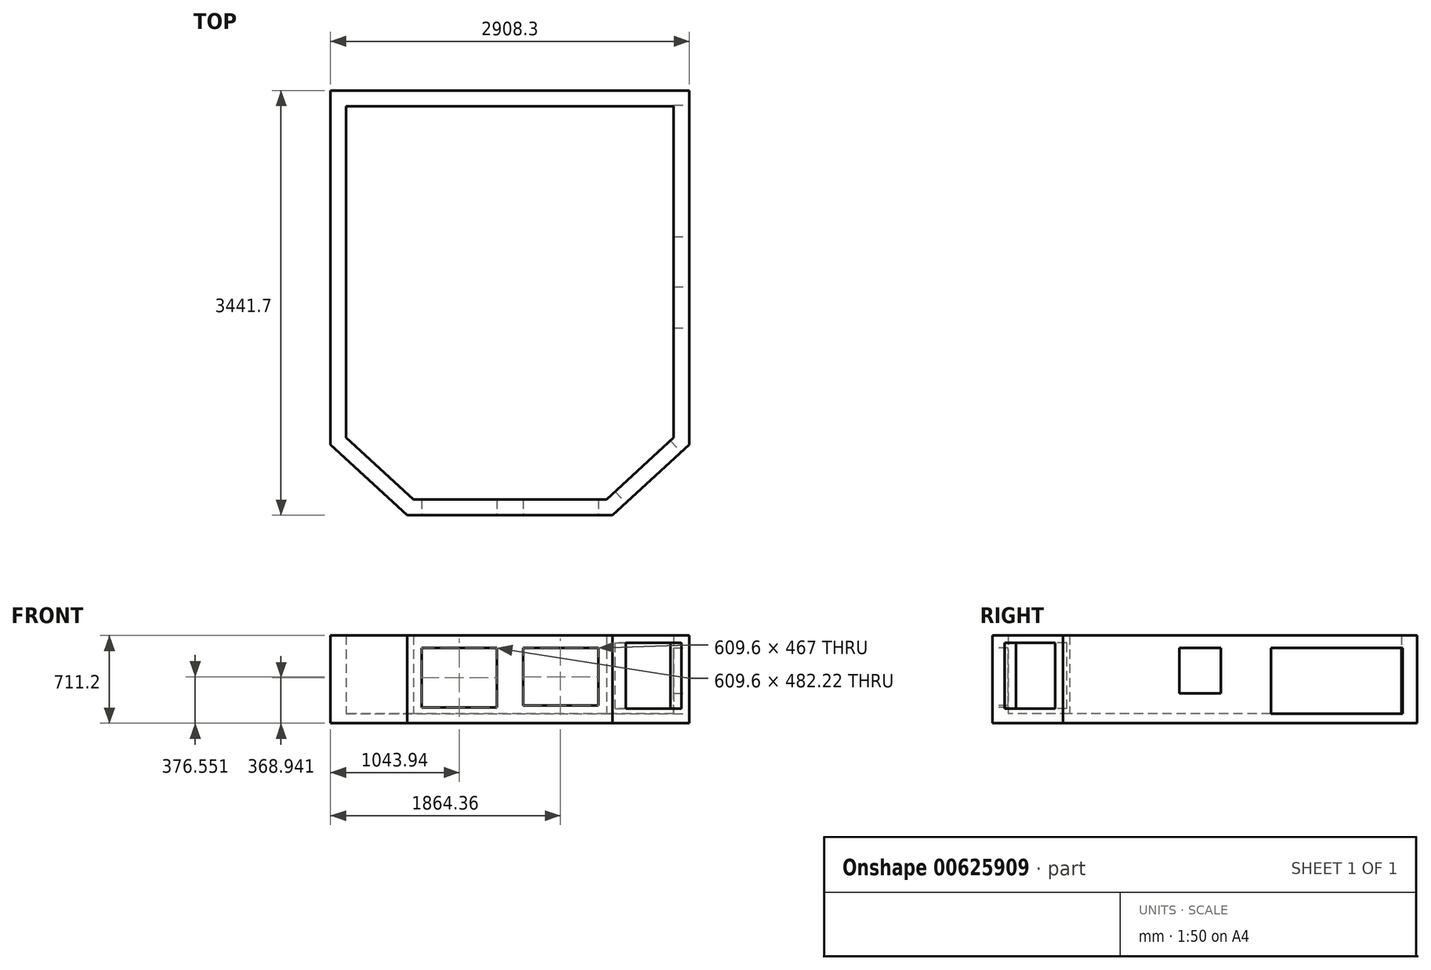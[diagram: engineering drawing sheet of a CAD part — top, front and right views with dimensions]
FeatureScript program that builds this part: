
annotation { "Feature Type Name" : "Feature", "Feature Type Description" : "" }
export const myFeature = defineFeature(function(context is Context, id is Id, definition is map)
    precondition{}
    {
        {
            var Q0;
            Q0=qCreatedBy(makeId("Top.planeOp"),FACE);
            var sketch = newSketch(context, id + "F0", { "sketchPlane" : qUnion([Q0])});
            skLineSegment(sketch, "E0", {"start": v(0, 0) * mm, "end": v(2908.3, 0) * mm});
            skLineSegment(sketch, "E1", {"start": v(2908.3, 0) * mm, "end": v(2908.3, -2870.2) * mm});
            skLineSegment(sketch, "E2", {"start": v(2908.3, -2870.2) * mm, "end": v(2286, -3441.7) * mm});
            skLineSegment(sketch, "E3", {"start": v(2286, -3441.7) * mm, "end": v(622.3, -3441.7) * mm});
            skLineSegment(sketch, "E4", {"start": v(622.3, -3441.7) * mm, "end": v(0, -2870.2) * mm});
            skLineSegment(sketch, "E5", {"start": v(0, 0) * mm, "end": v(0, -2870.2) * mm});
            skSolve(sketch);
        }
        {
            var Q0;
            Q0=makeQuery(id+"F0.imprint","IMPRINT",FACE,{"disambiguationData":[TD([[makeQuery(id+"F0.imprint","IMPRINT",EDGE,{"derivedFrom":sQuery(id+"F0.wireOp",EDGE,"E0")}),-1.0]])]});
            extrude(context, id + "F1", {"entities" : qUnion([Q0]), "oppositeDirection" : true, "depth" : 76.2 * mm, "offsetDistance" : 25.4 * mm});
        }
        {
            var Q0;
            Q0=makeQuery(id+"F1.opExtrude","CAP_FACE",FACE,{"disambiguationData":[OSD([sQuery(id+"F0.wireOp",EDGE,"E0"),sQuery(id+"F0.wireOp",EDGE,"E1"),sQuery(id+"F0.wireOp",EDGE,"E2"),sQuery(id+"F0.wireOp",EDGE,"E3"),sQuery(id+"F0.wireOp",EDGE,"E4"),sQuery(id+"F0.wireOp",EDGE,"E5")])],"isStart":true});
            var sketch = newSketch(context, id + "F2", { "sketchPlane" : qUnion([Q0])});
            skLineSegment(sketch, "E6.0", {"start": v(127, -127) * mm, "end": v(127, -2814.4) * mm});
            skLineSegment(sketch, "E6.1", {"start": v(2781.3, -127) * mm, "end": v(2781.3, -2814.4) * mm});
            skLineSegment(sketch, "E6.2", {"start": v(2781.3, -2814.4) * mm, "end": v(2236.53, -3314.7) * mm});
            skLineSegment(sketch, "E6.3", {"start": v(127, -127) * mm, "end": v(2781.3, -127) * mm});
            skLineSegment(sketch, "E6.4", {"start": v(2236.53, -3314.7) * mm, "end": v(671.77, -3314.7) * mm});
            skLineSegment(sketch, "E6.5", {"start": v(671.77, -3314.7) * mm, "end": v(127, -2814.4) * mm});
            skSolve(sketch);
        }
        {
            var Q0;
            Q0=makeQuery(id+"F2.imprint","IMPRINT",FACE,{"disambiguationData":[TD([[makeQuery(id+"F2.imprint","IMPRINT",EDGE,{"derivedFrom":sQuery(id+"F2.wireOp",EDGE,"E6.0")}),-1.0]])]});
            extrude(context, id + "F3", {"entities" : qUnion([Q0]), "operationType" : NewBodyOperationType.ADD, "depth" : 635 * mm, "offsetDistance" : 25.4 * mm});
        }
        {
            var Q0;
            {var subQ0=sQuery(id+"F0.wireOp",EDGE,"E1");Q0=makeQuery(id+"F3.boolean.opBoolean","MERGE",FACE,{"derivedFrom":[makeQuery(id+"F1.opExtrude","SWEPT_FACE",FACE,{"disambiguationData":[OSD([subQ0])]}),makeQuery(id+"F3.opExtrude","SWEPT_FACE",FACE,{"disambiguationData":[OSD([subQ0])]})]});}
            var sketch = newSketch(context, id + "F4", { "sketchPlane" : qUnion([Q0])});
            skLineSegment(sketch, "E7.bottom", {"start": v(-1925.32, 533.4) * mm, "end": v(-1590.04, 533.4) * mm});
            skLineSegment(sketch, "E7.top", {"start": v(-1925.32, 165.1) * mm, "end": v(-1590.04, 165.1) * mm});
            skLineSegment(sketch, "E7.left", {"start": v(-1925.32, 533.4) * mm, "end": v(-1925.32, 165.1) * mm});
            skLineSegment(sketch, "E7.right", {"start": v(-1590.04, 533.4) * mm, "end": v(-1590.04, 165.1) * mm});
            skLineSegment(sketch, "E8.bottom", {"start": v(-1183.64, 533.4) * mm, "end": v(-116.84, 533.4) * mm});
            skLineSegment(sketch, "E8.top", {"start": v(-1183.64, 0) * mm, "end": v(-116.84, 0) * mm});
            skLineSegment(sketch, "E8.left", {"start": v(-1183.64, 533.4) * mm, "end": v(-1183.64, 0) * mm});
            skLineSegment(sketch, "E8.right", {"start": v(-116.84, 533.4) * mm, "end": v(-116.84, 0) * mm});
            skSolve(sketch);
        }
        {
            var Q0;
            {var subQ0=sQuery(id+"F0.wireOp",EDGE,"E2");Q0=makeQuery(id+"F3.boolean.opBoolean","MERGE",FACE,{"derivedFrom":[makeQuery(id+"F1.opExtrude","SWEPT_FACE",FACE,{"disambiguationData":[OSD([subQ0])]}),makeQuery(id+"F3.opExtrude","SWEPT_FACE",FACE,{"disambiguationData":[OSD([subQ0])]})]});}
            var sketch = newSketch(context, id + "F5", { "sketchPlane" : qUnion([Q0])});
            skLineSegment(sketch, "E9.bottom", {"start": v(-498.63, 573.72) * mm, "end": v(110.97, 573.72) * mm});
            skLineSegment(sketch, "E9.top", {"start": v(-498.63, 40.32) * mm, "end": v(110.97, 40.32) * mm});
            skLineSegment(sketch, "E9.left", {"start": v(-498.63, 573.72) * mm, "end": v(-498.63, 40.32) * mm});
            skLineSegment(sketch, "E9.right", {"start": v(110.97, 573.72) * mm, "end": v(110.97, 40.32) * mm});
            skSolve(sketch);
        }
        {
            var Q0;
            Q0=makeQuery(id+"F4.imprint","IMPRINT",FACE,{"disambiguationData":[TD([[makeQuery(id+"F4.imprint","IMPRINT",EDGE,{"derivedFrom":sQuery(id+"F4.wireOp",EDGE,"E8.bottom")}),-1.0]])]});
            var Q1;
            Q1=makeQuery(id+"F4.imprint","IMPRINT",FACE,{"disambiguationData":[TD([[makeQuery(id+"F4.imprint","IMPRINT",EDGE,{"derivedFrom":sQuery(id+"F4.wireOp",EDGE,"E7.bottom")}),-1.0]])]});
            var Q2;
            Q2=makeQuery(id+"F3.opExtrude","SWEPT_FACE",FACE,{"disambiguationData":[OSD([sQuery(id+"F2.wireOp",EDGE,"E6.1")])]});
            extrude(context, id + "F6", {"entities" : qUnion([Q0, Q1]), "operationType" : NewBodyOperationType.REMOVE, "endBound" : BoundingType.UP_TO_SURFACE, "oppositeDirection" : true, "depth" : 25.4 * mm, "endBoundEntityFace" : qUnion([Q2]), "offsetDistance" : 25.4 * mm});
        }
        {
            var Q0;
            Q0=makeQuery(id+"F5.imprint","IMPRINT",FACE,{"disambiguationData":[TD([[makeQuery(id+"F5.imprint","IMPRINT",EDGE,{"derivedFrom":sQuery(id+"F5.wireOp",EDGE,"E9.bottom")}),-1.0]])]});
            var Q1;
            Q1=makeQuery(id+"F3.opExtrude","SWEPT_FACE",FACE,{"disambiguationData":[OSD([sQuery(id+"F2.wireOp",EDGE,"E6.2")])]});
            extrude(context, id + "F7", {"entities" : qUnion([Q0]), "operationType" : NewBodyOperationType.REMOVE, "endBound" : BoundingType.UP_TO_SURFACE, "oppositeDirection" : true, "depth" : 25.4 * mm, "endBoundEntityFace" : qUnion([Q1]), "offsetDistance" : 25.4 * mm});
        }
        {
            var Q0;
            {var subQ0=sQuery(id+"F0.wireOp",EDGE,"E3");Q0=makeQuery(id+"F3.boolean.opBoolean","MERGE",FACE,{"derivedFrom":[makeQuery(id+"F1.opExtrude","SWEPT_FACE",FACE,{"disambiguationData":[OSD([subQ0])]}),makeQuery(id+"F3.opExtrude","SWEPT_FACE",FACE,{"disambiguationData":[OSD([subQ0])]})]});}
            var sketch = newSketch(context, id + "F8", { "sketchPlane" : qUnion([Q0])});
            skLineSegment(sketch, "E10.bottom", {"start": v(739.14, 533.85) * mm, "end": v(1348.74, 533.85) * mm});
            skLineSegment(sketch, "E10.top", {"start": v(739.14, 51.63) * mm, "end": v(1348.74, 51.63) * mm});
            skLineSegment(sketch, "E10.left", {"start": v(739.14, 533.85) * mm, "end": v(739.14, 51.63) * mm});
            skLineSegment(sketch, "E10.right", {"start": v(1348.74, 533.85) * mm, "end": v(1348.74, 51.63) * mm});
            skLineSegment(sketch, "E11.bottom", {"start": v(1348.74, 51.63) * mm, "end": v(1348.74, 51.63) * mm});
            skLineSegment(sketch, "E11.top", {"start": v(1348.74, 200.24) * mm, "end": v(1348.74, 200.24) * mm});
            skLineSegment(sketch, "E11.left", {"start": v(1348.74, 51.63) * mm, "end": v(1348.74, 200.24) * mm});
            skLineSegment(sketch, "E11.right", {"start": v(1348.74, 51.63) * mm, "end": v(1348.74, 200.24) * mm});
            skSolve(sketch);
        }
        {
            var Q0;
            Q0 = qSketchRegion(id + "F8", true);
            var Q1;
            Q1=makeQuery(id+"F3.opExtrude","SWEPT_FACE",FACE,{"disambiguationData":[OSD([sQuery(id+"F2.wireOp",EDGE,"E6.4")])]});
            extrude(context, id + "F9", {"entities" : qUnion([Q0]), "operationType" : NewBodyOperationType.REMOVE, "endBound" : BoundingType.UP_TO_SURFACE, "oppositeDirection" : true, "depth" : 25.4 * mm, "endBoundEntityFace" : qUnion([Q1]), "offsetDistance" : 25.4 * mm});
        }
        {
            var Q0;
            Q0=makeQuery(id+"F8.imprint","IMPRINT",FACE,{"disambiguationData":[TD([[makeQuery(id+"F8.imprint","IMPRINT",EDGE,{"derivedFrom":sQuery(id+"F8.wireOp",EDGE,"E10.bottom")}),1.0]])]});
            var sketch = newSketch(context, id + "F10", { "sketchPlane" : qUnion([Q0])});
            skLineSegment(sketch, "E12.bottom", {"start": v(1559.56, 533.85) * mm, "end": v(2169.16, 533.85) * mm});
            skLineSegment(sketch, "E12.top", {"start": v(1559.56, 66.85) * mm, "end": v(2169.16, 66.85) * mm});
            skLineSegment(sketch, "E12.left", {"start": v(1559.56, 533.85) * mm, "end": v(1559.56, 66.85) * mm});
            skLineSegment(sketch, "E12.right", {"start": v(2169.16, 533.85) * mm, "end": v(2169.16, 66.85) * mm});
            skSolve(sketch);
        }
        {
            var Q0;
            Q0 = qSketchRegion(id + "F10", true);
            var Q1;
            Q1=makeQuery(id+"F3.opExtrude","SWEPT_FACE",FACE,{"disambiguationData":[OSD([sQuery(id+"F2.wireOp",EDGE,"E6.4")])]});
            extrude(context, id + "F11", {"entities" : qUnion([Q0]), "operationType" : NewBodyOperationType.REMOVE, "endBound" : BoundingType.UP_TO_SURFACE, "oppositeDirection" : true, "depth" : 25.4 * mm, "endBoundEntityFace" : qUnion([Q1]), "offsetDistance" : 25.4 * mm});
        }
    });
